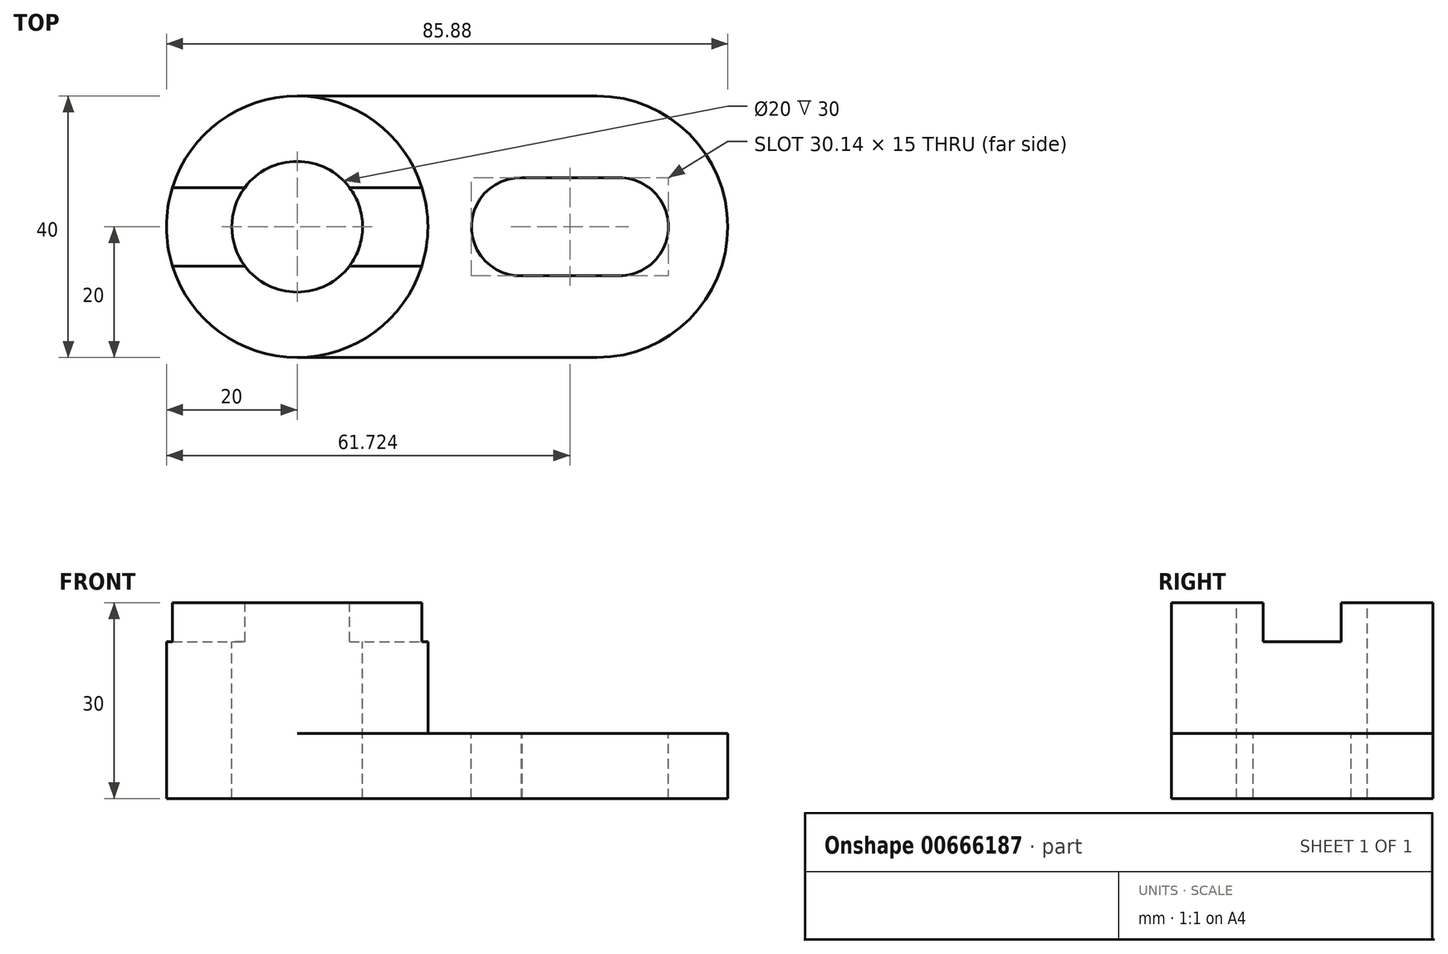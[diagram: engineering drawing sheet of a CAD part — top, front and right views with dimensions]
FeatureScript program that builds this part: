
annotation { "Feature Type Name" : "Feature", "Feature Type Description" : "" }
export const myFeature = defineFeature(function(context is Context, id is Id, definition is map)
    precondition{}
    {
        {
            var Q0;
            Q0=qCreatedBy(makeId("Top.planeOp"),FACE);
            var sketch = newSketch(context, id + "F0", { "sketchPlane" : qUnion([Q0])});
            skArc(sketch, "E0", {"start": v(0, 20) * mm, "mid": v(-20, 0) * mm, "end": v(0, -20) * mm});
            skArc(sketch, "E1", {"start": v(45.88, -20) * mm, "mid": v(65.88, 0) * mm, "end": v(45.88, 20) * mm});
            skLineSegment(sketch, "E2", {"start": v(0, 20) * mm, "end": v(45.88, 20) * mm});
            skLineSegment(sketch, "E3", {"start": v(0, -20) * mm, "end": v(45.88, -20) * mm});
            skSolve(sketch);
        }
        {
            var Q0;
            Q0 = qSketchRegion(id + "F0", true);
            extrude(context, id + "F1", {"entities" : qUnion([Q0]), "depth" : 10 * mm, "offsetDistance" : 25 * mm});
        }
        {
            var Q0;
            Q0=makeQuery(id+"F1.opExtrude","CAP_FACE",FACE,{"disambiguationData":[OSD([sQuery(id+"F0.wireOp",EDGE,"E0"),sQuery(id+"F0.wireOp",EDGE,"E1"),sQuery(id+"F0.wireOp",EDGE,"E2"),sQuery(id+"F0.wireOp",EDGE,"E3")])],"isStart":false});
            var sketch = newSketch(context, id + "F2", { "sketchPlane" : qUnion([Q0])});
            skCircle(sketch, "E4", {"center": v(0, 0) * mm, "radius": 20 * mm});
            skSolve(sketch);
        }
        {
            var Q0;
            {var subQ0=sQuery(id+"F2.wireOp",EDGE,"E4");var subQ1=makeQuery(id+"F2.imprint","INTERSECT",VERTEX,{"derivedFrom":[makeQuery(id+"F1.opExtrude","CAP_EDGE",EDGE,{"disambiguationData":[OSD([sQuery(id+"F0.wireOp",EDGE,"E2")])],"isStart":false}),subQ0]});Q0=makeQuery(id+"F2.imprint","IMPRINT",FACE,{"disambiguationData":[TD([[makeQuery(id+"F2.imprint","IMPRINT",EDGE,{"disambiguationData":[TD([[subQ1,-1.0]])],"derivedFrom":subQ0}),1.0]])]});}
            extrude(context, id + "F3", {"entities" : qUnion([Q0]), "operationType" : NewBodyOperationType.ADD, "depth" : 20 * mm, "offsetDistance" : 25 * mm});
        }
        {
            var Q0;
            Q0=makeQuery(id+"F3.opExtrude","CAP_FACE",FACE,{"disambiguationData":[OSD([sQuery(id+"F2.wireOp",EDGE,"E4")])],"isStart":false});
            var sketch = newSketch(context, id + "F4", { "sketchPlane" : qUnion([Q0])});
            skCircle(sketch, "E5", {"center": v(0, 0) * mm, "radius": 10 * mm});
            skSolve(sketch);
        }
        {
            var Q0;
            Q0 = qSketchRegion(id + "F4", true);
            extrude(context, id + "F5", {"entities" : qUnion([Q0]), "operationType" : NewBodyOperationType.REMOVE, "oppositeDirection" : true, "depth" : 93.7 * mm, "offsetDistance" : 25 * mm});
        }
        {
            var Q0;
            Q0=makeQuery(id+"F3.opExtrude","CAP_FACE",FACE,{"disambiguationData":[OSD([sQuery(id+"F2.wireOp",EDGE,"E4")])],"isStart":false});
            var sketch = newSketch(context, id + "F6", { "sketchPlane" : qUnion([Q0])});
            skLineSegment(sketch, "E6.bottom", {"start": v(-25, 6) * mm, "end": v(25, 6) * mm});
            skLineSegment(sketch, "E6.top", {"start": v(-25, -6) * mm, "end": v(25, -6) * mm});
            skLineSegment(sketch, "E6.left", {"start": v(-25, 6) * mm, "end": v(-25, -6) * mm});
            skLineSegment(sketch, "E6.right", {"start": v(25, 6) * mm, "end": v(25, -6) * mm});
            skSolve(sketch);
        }
        {
            var Q0;
            Q0 = qSketchRegion(id + "F6", true);
            extrude(context, id + "F7", {"entities" : qUnion([Q0]), "operationType" : NewBodyOperationType.REMOVE, "oppositeDirection" : true, "depth" : 6 * mm, "offsetDistance" : 25 * mm});
        }
        {
            var Q0;
            Q0=makeQuery(id+"F1.opExtrude","CAP_FACE",FACE,{"disambiguationData":[OSD([sQuery(id+"F0.wireOp",EDGE,"E0"),sQuery(id+"F0.wireOp",EDGE,"E1"),sQuery(id+"F0.wireOp",EDGE,"E2"),sQuery(id+"F0.wireOp",EDGE,"E3")])],"isStart":false});
            var sketch = newSketch(context, id + "F8", { "sketchPlane" : qUnion([Q0])});
            skArc(sketch, "E7", {"start": v(34.3, 7.5) * mm, "mid": v(26.65, -0.06) * mm, "end": v(34.42, -7.5) * mm});
            skArc(sketch, "E8", {"start": v(49.3, -7.5) * mm, "mid": v(56.8, 0) * mm, "end": v(49.3, 7.5) * mm});
            skLineSegment(sketch, "E9", {"start": v(34.3, 7.5) * mm, "end": v(49.3, 7.5) * mm});
            skLineSegment(sketch, "E10", {"start": v(33.88, -7.5) * mm, "end": v(49.3, -7.5) * mm});
            skSolve(sketch);
        }
        {
            var Q0;
            {var subQ5=sQuery(id+"F8.wireOp",EDGE,"E8");Q0=makeQuery(id+"F8.imprint","IMPRINT",FACE,{"disambiguationData":[TD([[makeQuery(id+"F8.imprint","IMPRINT",EDGE,{"derivedFrom":subQ5}),1.0]])]});}
            var sketch = newSketch(context, id + "F9", { "sketchPlane" : qUnion([Q0])});
            skSolve(sketch);
        }
        {
            var Q0;
            Q0 = qSketchRegion(id + "F8", true);
            var Q1;
            {var subQ5=sQuery(id+"F8.wireOp",EDGE,"E8");Q1=makeQuery(id+"F9.imprint","IMPRINT",FACE,{"disambiguationData":[TD([[makeQuery(id+"F9.imprint","IMPRINT",EDGE,{"derivedFrom":makeQuery(id+"F8.imprint","IMPRINT",EDGE,{"derivedFrom":subQ5})}),1.0]])]});}
            extrude(context, id + "F10", {"entities" : qUnion([Q0, Q1]), "operationType" : NewBodyOperationType.REMOVE, "oppositeDirection" : true, "depth" : 28.9 * mm, "offsetDistance" : 25 * mm});
        }
    });
